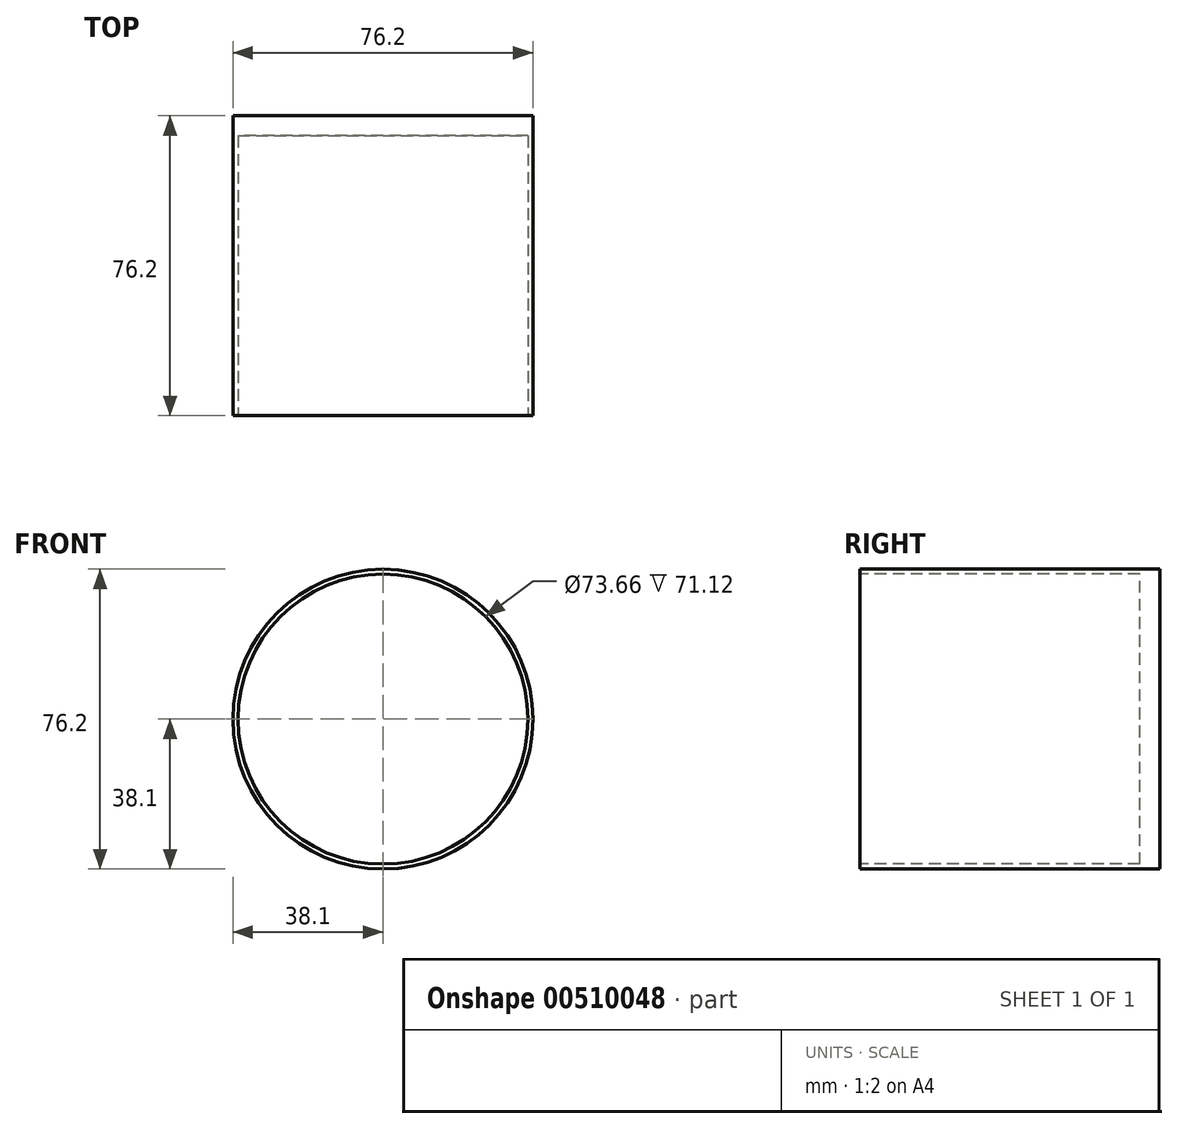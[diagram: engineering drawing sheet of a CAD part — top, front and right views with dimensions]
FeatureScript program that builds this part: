
annotation { "Feature Type Name" : "Feature", "Feature Type Description" : "" }
export const myFeature = defineFeature(function(context is Context, id is Id, definition is map)
    precondition{}
    {
        {
            var Q0;
            Q0=qCreatedBy(makeId("Front.planeOp"),FACE);
            var sketch = newSketch(context, id + "F0", { "sketchPlane" : qUnion([Q0])});
            skCircle(sketch, "E0", {"center": v(0, 0) * mm, "radius": 38.1 * mm});
            skSolve(sketch);
        }
        {
            var Q0;
            Q0=qSketchRegion(id+"F0",true);
            extrude(context, id + "F1", {"entities" : qUnion([Q0]), "depth" : 76.2 * mm});
        }
        {
            var Q0;
            Q0=makeQuery(id+"F1.opExtrude","CAP_FACE",FACE,{"disambiguationData":[OSD([sQuery(id+"F0.wireOp",EDGE,"E0")])],"isStart":false});
            var sketch = newSketch(context, id + "F2", { "sketchPlane" : qUnion([Q0])});
            skCircle(sketch, "E1", {"center": v(0, 0) * mm, "radius": 36.83 * mm});
            skSolve(sketch);
        }
        {
            var Q0;
            Q0=qSketchRegion(id+"F2",true);
            extrude(context, id + "F3", {"entities" : qUnion([Q0]), "operationType" : NewBodyOperationType.REMOVE, "oppositeDirection" : true, "depth" : 71.12 * mm});
        }
    });
